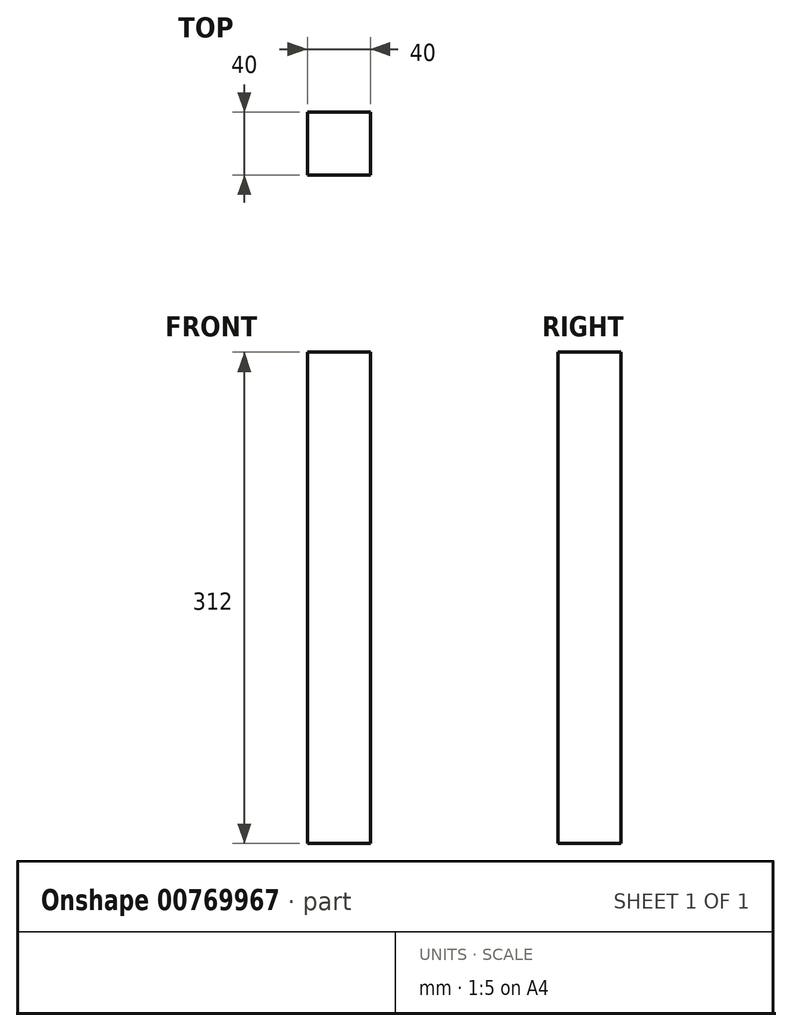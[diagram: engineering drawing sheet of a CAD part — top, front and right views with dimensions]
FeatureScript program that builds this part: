
annotation { "Feature Type Name" : "Feature", "Feature Type Description" : "" }
export const myFeature = defineFeature(function(context is Context, id is Id, definition is map)
    precondition{}
    {
        {
            var Q0;
            Q0=qCreatedBy(makeId("Top.planeOp"),FACE);
            var sketch = newSketch(context, id + "F0", { "sketchPlane" : qUnion([Q0])});
            skLineSegment(sketch, "E0.bottom", {"start": v(20, -20) * mm, "end": v(-20, -20) * mm});
            skLineSegment(sketch, "E0.top", {"start": v(20, 20) * mm, "end": v(-20, 20) * mm});
            skLineSegment(sketch, "E0.left", {"start": v(20, -20) * mm, "end": v(20, 20) * mm});
            skLineSegment(sketch, "E0.right", {"start": v(-20, -20) * mm, "end": v(-20, 20) * mm});
            skPoint(sketch, "E0.middle", {"position": v(0, 0) * mm});
            skSolve(sketch);
        }
        {
            var Q0;
            Q0 = qSketchRegion(id + "F0", true);
            extrude(context, id + "F1", {"entities" : qUnion([Q0]), "depth" : 312 * mm, "offsetDistance" : 25 * mm});
        }
    });
